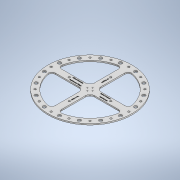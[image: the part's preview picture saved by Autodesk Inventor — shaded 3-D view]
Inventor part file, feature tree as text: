
AUTODESK INVENTOR PART (.ipt)
format: ipt  version: 2020.2 (Build 242310000, 310)  size: 1,957,888 bytes
history: native  units: mm
features: sketch x6, hole x3, extrude x2
ambient origin geometry x8: Origin, YZ Plane, XZ Plane, XY Plane, X Axis, Y Axis, Z Axis, Center Point
bodies: Solido1 (feature_tree)
feature tree (11):
  extrude  "Estrusione1"  Depth=260.0mm
  hole  "Foro1"  [1 undecoded]
  hole  "Foro2"  [1 undecoded]
  hole  "Foro3"  [1 undecoded]
  extrude  "Estrusione2"  Depth=40.0mm TaperAngle=360.0deg
  sketch  "Schizzo 3D1"
  sketch  "Schizzo1"
  sketch  "Schizzo2"
  sketch  "Schizzo3"
  sketch  "Schizzo4"
  sketch  "Schizzo5"
note: 3 required parameter values undecoded (feature->parameter linkage not recoverable at this tier; creation-order binding heuristic only, values carry confidence <= 0.55)
